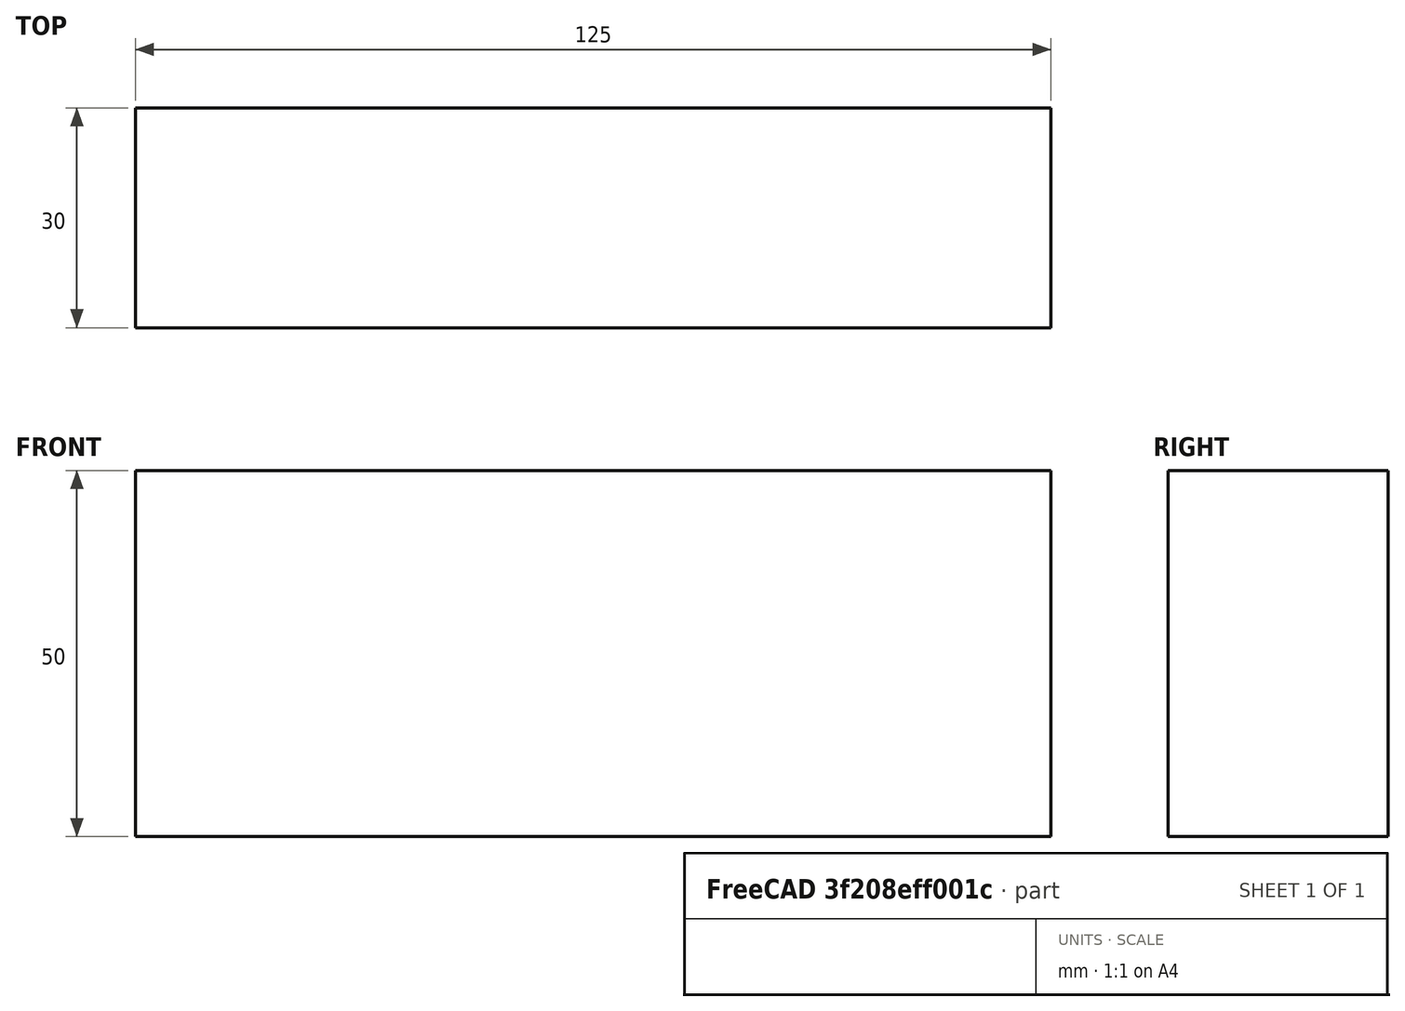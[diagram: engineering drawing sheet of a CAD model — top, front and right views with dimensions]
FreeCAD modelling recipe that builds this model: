
FCSTD DOCUMENT  (FreeCAD 0.15R4671 (Git))
Label: Flat Bar 125x30 EN10058 S235JR
License: All rights reserved
LicenseURL: http://en.wikipedia.org/wiki/All_rights_reserved
objects: Sketcher::SketchObject×1, Part::Extrusion×1
note: 2 computed .brp shape members not serialized (recipe doc carries the construction recipe); baked Part::Feature solids carry a one-line shape summary decoded from their .brp

FEATURE [Sketcher::SketchObject] Sketch
  sketch-geometry (4):
    g0: LineSegment StartX=-62.5 StartY=-15 StartZ=0 EndX=62.5 EndY=-15 EndZ=0
    g1: LineSegment StartX=62.5 StartY=-15 StartZ=0 EndX=62.5 EndY=15 EndZ=0
    g2: LineSegment StartX=62.5 StartY=15 StartZ=0 EndX=-62.5 EndY=15 EndZ=0
    g3: LineSegment StartX=-62.5 StartY=15 StartZ=0 EndX=-62.5 EndY=-15 EndZ=0
  constraints (12):
    c: Coincident(g0,g1)
    c: Coincident(g1,g2)
    c: Coincident(g2,g3)
    c: Coincident(g3,g0)
    c: Horizontal(g0)
    c: Horizontal(g2)
    c: Vertical(g1)
    c: Vertical(g3)
    c: Symmetric(g1,g2,g-2)
    c: Symmetric(g0,g1,g-1)
    c: DistanceY(g1) = 30
    c: DistanceX(g0) = 125
FEATURE [Part::Extrusion] Extrude  label="Flat Bar 125x30 EN10058 S235JR"
  Base = -> Sketch
  Dir = (0,0,50)
  Solid = true
